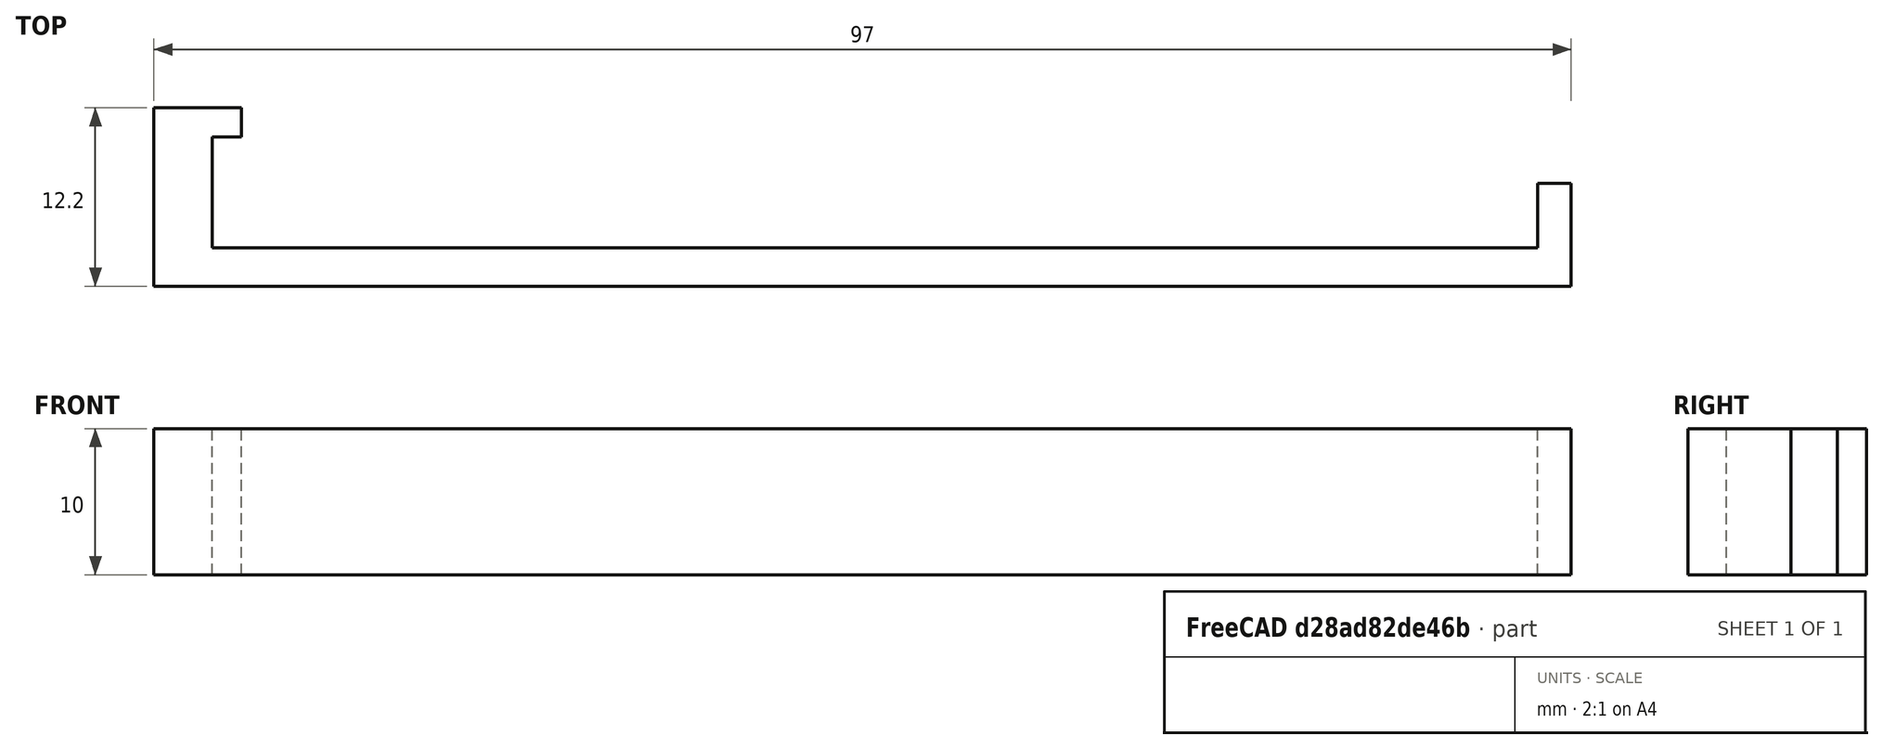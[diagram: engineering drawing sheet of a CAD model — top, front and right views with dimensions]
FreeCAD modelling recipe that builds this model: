
FCSTD DOCUMENT  (FreeCAD 0.19R)
Label: Winch
License: All rights reserved
LicenseURL: http://en.wikipedia.org/wiki/All_rights_reserved
objects: Sketcher::SketchObject×1, PartDesign::Pad×1, PartDesign::Body×1
note: 4 computed .brp shape members not serialized (recipe doc carries the construction recipe); baked Part::Feature solids carry a one-line shape summary decoded from their .brp

FEATURE [Sketcher::SketchObject] Sketch
  FullyConstrained = false
  MapMode = 5
  Support = -> [XY_Plane]
  sketch-geometry (10):
    g0: LineSegment StartX=0 StartY=0 StartZ=0 EndX=97 EndY=0 EndZ=0
    g1: LineSegment StartX=0 StartY=0 StartZ=0 EndX=0 EndY=12.2 EndZ=0
    g2: LineSegment StartX=4 StartY=2.6325 StartZ=0 EndX=4 EndY=10.2 EndZ=0
    g3: LineSegment StartX=4 StartY=10.2 StartZ=0 EndX=6 EndY=10.2 EndZ=0
    g4: LineSegment StartX=6 StartY=10.2 StartZ=0 EndX=6 EndY=12.2 EndZ=0
    g5: LineSegment StartX=6 StartY=12.2 StartZ=0 EndX=0 EndY=12.2 EndZ=0
    g6: LineSegment StartX=97 StartY=0 StartZ=0 EndX=97 EndY=7.02511 EndZ=0
    g7: LineSegment StartX=4 StartY=2.6325 StartZ=0 EndX=94.6934 EndY=2.6325 EndZ=0
    g8: LineSegment StartX=94.6934 StartY=2.6325 StartZ=0 EndX=94.6934 EndY=7.02511 EndZ=0
    g9: LineSegment StartX=94.6934 StartY=7.02511 StartZ=0 EndX=97 EndY=7.02511 EndZ=0
  constraints (26):
    c: Horizontal(g0)
    c: Vertical(g1)
    c: Vertical(g2)
    c: DistanceY(g-1,g2) = 10.2
    c: Coincident(g3,g2)
    c: Horizontal(g3)
    c: Coincident(g4,g3)
    c: Vertical(g4)
    c: Coincident(g5,g4)
    c: Coincident(g5,g1)
    c: Horizontal(g5)
    c: DistanceY(g4,g4) = 2
    c: DistanceX(g2,g3) = 2
    c: DistanceX(g1,g2) = 4
    c: DistanceX(g0,g0) = 97
    c: Coincident(g6,g0)
    c: Vertical(g6)
    c: Coincident(g1,g-1)
    c: Coincident(g7,g2)
    c: Horizontal(g7)
    c: Coincident(g8,g7)
    c: Vertical(g8)
    c: Coincident(g9,g8)
    c: Coincident(g9,g6)
    c: Horizontal(g9)
    c: Coincident(g0,g1)
FEATURE [PartDesign::Pad] Pad
  Direction = (1,1,1)
  Length = 10
  Length2 = 100
  Profile = -> Sketch
  Type = 0
FEATURE [PartDesign::Body] Body
  Group = -> [Sketch,Pad]
  Origin = -> Origin
  Tip = -> Pad
